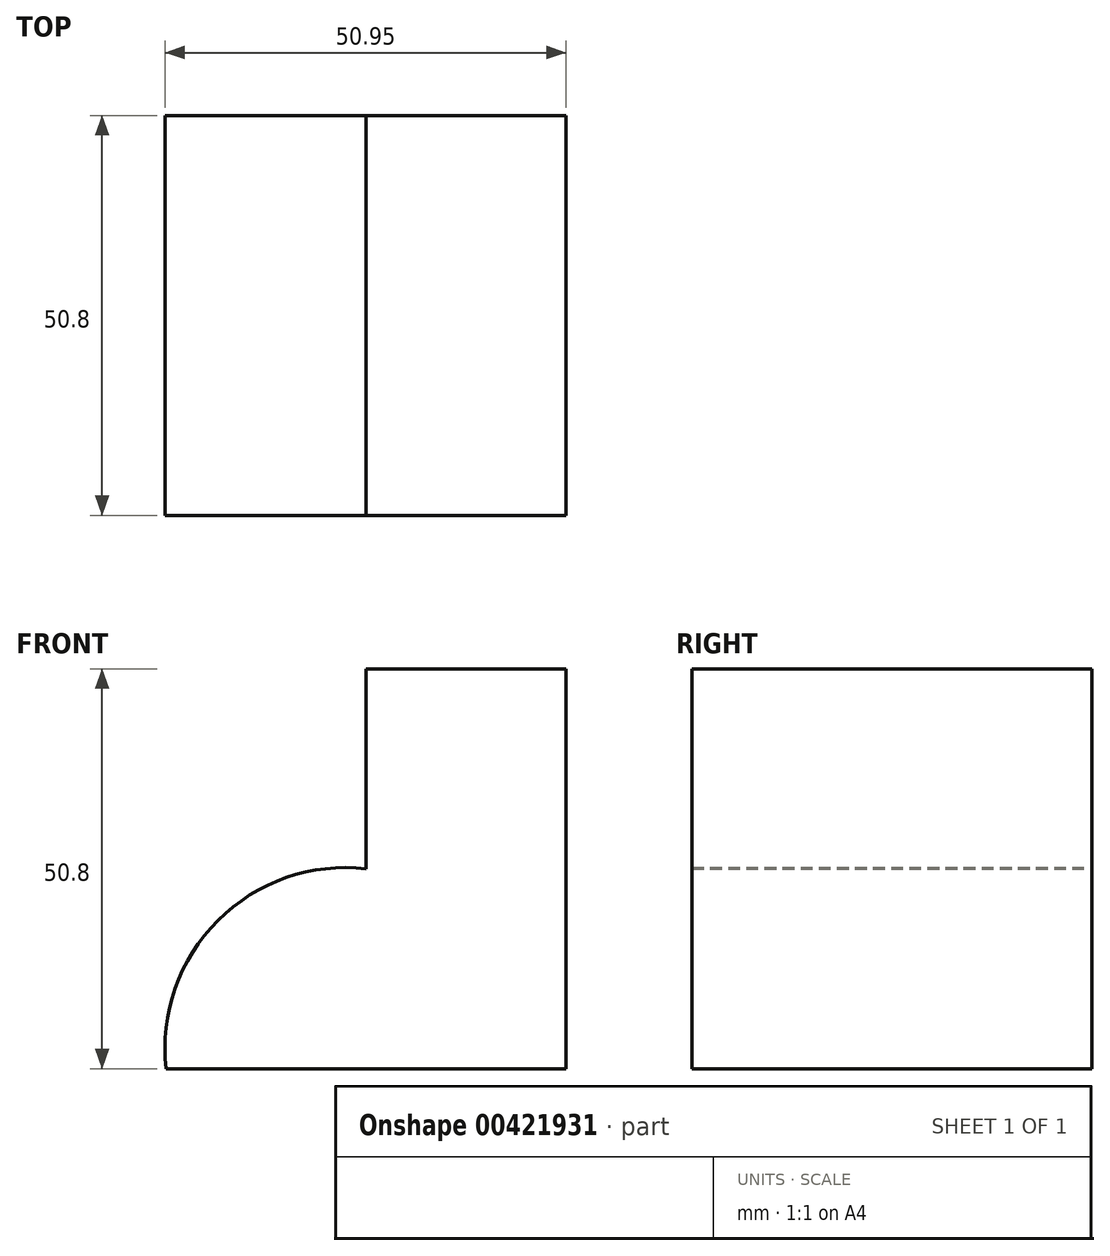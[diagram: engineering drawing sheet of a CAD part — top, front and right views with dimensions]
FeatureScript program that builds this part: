
annotation { "Feature Type Name" : "Feature", "Feature Type Description" : "" }
export const myFeature = defineFeature(function(context is Context, id is Id, definition is map)
    precondition{}
    {
        {
            var Q0;
            Q0=qCreatedBy(makeId("Front.planeOp"),FACE);
            var sketch = newSketch(context, id + "F0", { "sketchPlane" : qUnion([Q0])});
            skLineSegment(sketch, "E0", {"start": v(0, 0) * mm, "end": v(0, 50.8) * mm});
            skLineSegment(sketch, "E1", {"start": v(0, 50.8) * mm, "end": v(-25.4, 50.8) * mm});
            skLineSegment(sketch, "E2", {"start": v(-25.4, 50.8) * mm, "end": v(-25.4, 25.4) * mm});
            skLineSegment(sketch, "E3", {"start": v(-50.8, 0) * mm, "end": v(0, 0) * mm});
            skArc(sketch, "E4", {"start": v(-25.4, 25.4) * mm, "mid": v(-44.23, 18.83) * mm, "end": v(-50.8, 0) * mm});
            skSolve(sketch);
        }
        {
            var Q0;
            Q0=makeQuery(id+"F0.imprint","IMPRINT",FACE,{"disambiguationData":[TD([[makeQuery(id+"F0.imprint","IMPRINT",EDGE,{"derivedFrom":sQuery(id+"F0.wireOp",EDGE,"E0")}),1.0]])]});
            extrude(context, id + "F1", {"entities" : qUnion([Q0]), "depth" : 50.8 * mm});
        }
    });
